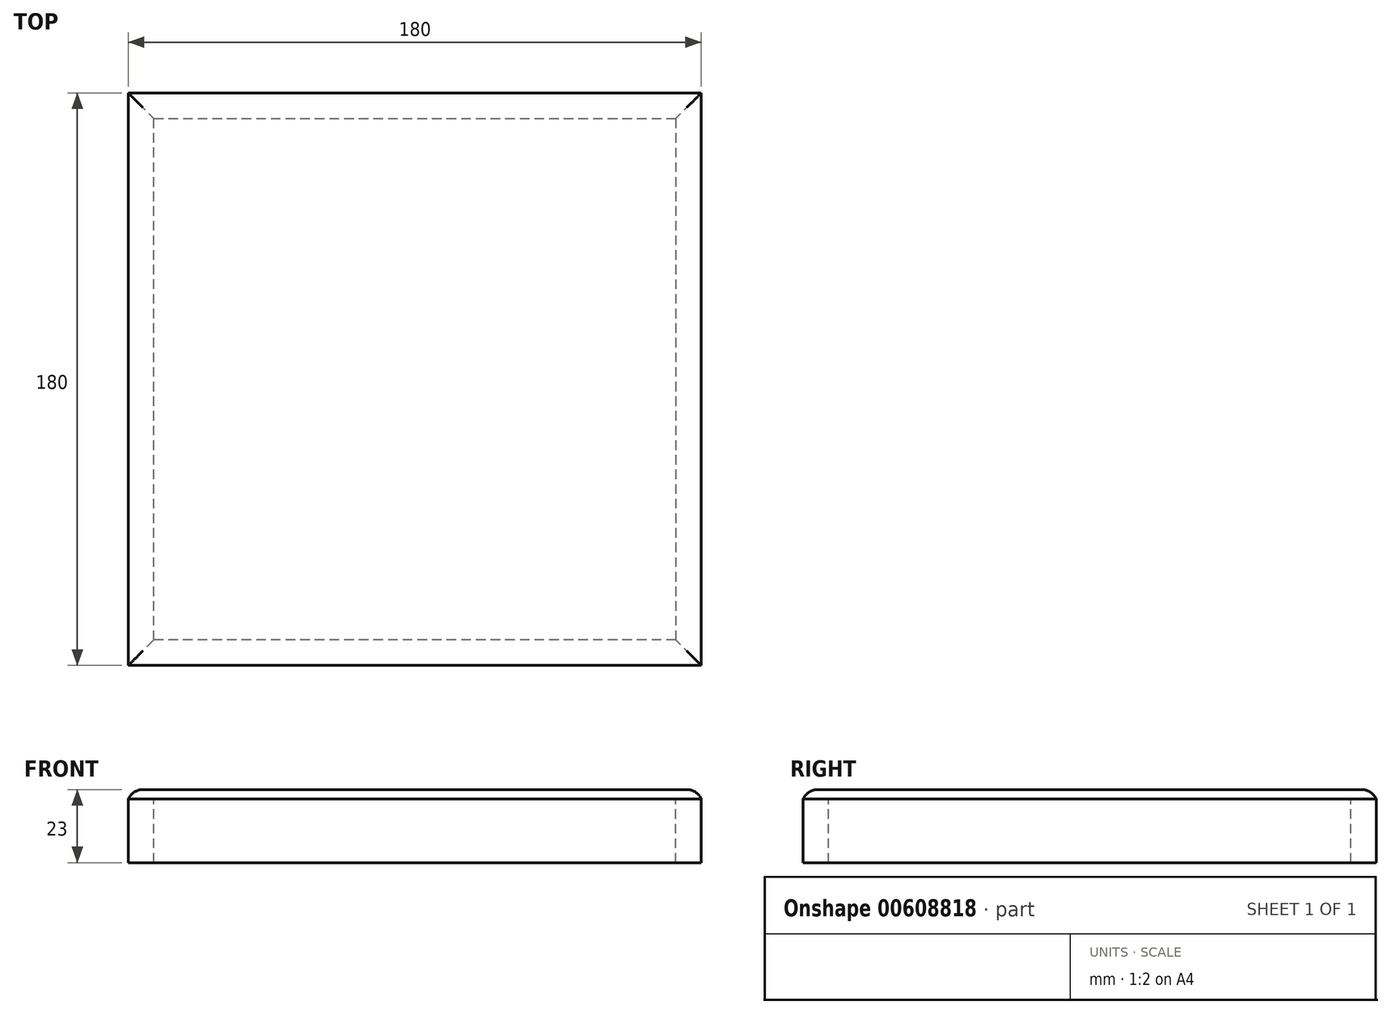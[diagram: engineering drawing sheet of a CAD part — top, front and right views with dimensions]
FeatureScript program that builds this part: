
annotation { "Feature Type Name" : "Feature", "Feature Type Description" : "" }
export const myFeature = defineFeature(function(context is Context, id is Id, definition is map)
    precondition{}
    {
        {
            var Q0;
            Q0=qCreatedBy(makeId("Top.planeOp"),FACE);
            var sketch = newSketch(context, id + "F0", { "sketchPlane" : qUnion([Q0])});
            skLineSegment(sketch, "E0.bottom", {"start": v(0, 0) * mm, "end": v(180, 0) * mm});
            skLineSegment(sketch, "E0.top", {"start": v(0, -180) * mm, "end": v(180, -180) * mm});
            skLineSegment(sketch, "E0.left", {"start": v(0, 0) * mm, "end": v(0, -180) * mm});
            skLineSegment(sketch, "E0.right", {"start": v(180, 0) * mm, "end": v(180, -180) * mm});
            skSolve(sketch);
        }
        {
            var Q0;
            Q0=makeQuery(id+"F0.imprint","IMPRINT",FACE,{"disambiguationData":[TD([[makeQuery(id+"F0.imprint","IMPRINT",EDGE,{"derivedFrom":sQuery(id+"F0.wireOp",EDGE,"E0.bottom")}),-1.0]])]});
            extrude(context, id + "F1", {"entities" : qUnion([Q0]), "oppositeDirection" : true, "depth" : 3 * mm, "offsetDistance" : 25 * mm});
        }
        {
            var Q0;
            Q0=makeQuery(id+"F1.opExtrude","CAP_FACE",FACE,{"disambiguationData":[OSD([sQuery(id+"F0.wireOp",EDGE,"E0.bottom"),sQuery(id+"F0.wireOp",EDGE,"E0.top"),sQuery(id+"F0.wireOp",EDGE,"E0.left"),sQuery(id+"F0.wireOp",EDGE,"E0.right")])],"isStart":false});
            var sketch = newSketch(context, id + "F2", { "sketchPlane" : qUnion([Q0])});
            skLineSegment(sketch, "E1.0", {"start": v(8, 172) * mm, "end": v(8, 8) * mm});
            skLineSegment(sketch, "E1.1", {"start": v(172, 172) * mm, "end": v(8, 172) * mm});
            skLineSegment(sketch, "E1.2", {"start": v(172, 8) * mm, "end": v(172, 172) * mm});
            skLineSegment(sketch, "E1.3", {"start": v(8, 8) * mm, "end": v(172, 8) * mm});
            skLineSegment(sketch, "E2", {"start": v(8, 172) * mm, "end": v(0, 180) * mm});
            skLineSegment(sketch, "E3", {"start": v(180, 180) * mm, "end": v(172, 172) * mm});
            skLineSegment(sketch, "E4", {"start": v(180, 0) * mm, "end": v(172, 8) * mm});
            skLineSegment(sketch, "E5", {"start": v(0, 0) * mm, "end": v(8, 8) * mm});
            skSolve(sketch);
        }
        {
            var Q0;
            Q0=makeQuery(id+"F2.imprint","IMPRINT",FACE,{"disambiguationData":[TD([[makeQuery(id+"F2.imprint","IMPRINT",EDGE,{"derivedFrom":sQuery(id+"F2.wireOp",EDGE,"E1.1")}),-1.0]])]});
            extrude(context, id + "F3", {"entities" : qUnion([Q0]), "depth" : 20 * mm, "offsetDistance" : 25 * mm});
        }
        {
            var Q0;
            Q0=makeQuery(id+"F2.imprint","IMPRINT",FACE,{"disambiguationData":[TD([[makeQuery(id+"F2.imprint","IMPRINT",EDGE,{"derivedFrom":sQuery(id+"F2.wireOp",EDGE,"E1.0")}),-1.0]])]});
            var Q1;
            Q1=makeQuery(id+"F3.opExtrude","CAP_VERTEX",VERTEX,{"disambiguationData":[OSD([sQuery(id+"F0.wireOp",EDGE,"E0.top"),sQuery(id+"F0.wireOp",EDGE,"E0.left"),sQuery(id+"F2.wireOp",EDGE,"E2")])],"isStart":false});
            extrude(context, id + "F4", {"entities" : qUnion([Q0]), "endBound" : BoundingType.UP_TO_VERTEX, "depth" : 25 * mm, "endBoundEntityVertex" : qUnion([Q1]), "offsetDistance" : 25 * mm});
        }
        {
            var Q0;
            Q0=makeQuery(id+"F2.imprint","IMPRINT",FACE,{"disambiguationData":[TD([[makeQuery(id+"F2.imprint","IMPRINT",EDGE,{"derivedFrom":sQuery(id+"F2.wireOp",EDGE,"E1.2")}),-1.0]])]});
            var Q1;
            Q1=makeQuery(id+"F3.opExtrude","CAP_VERTEX",VERTEX,{"disambiguationData":[OSD([sQuery(id+"F2.wireOp",EDGE,"E1.1"),sQuery(id+"F2.wireOp",EDGE,"E1.2"),sQuery(id+"F2.wireOp",EDGE,"E3")])],"isStart":false});
            extrude(context, id + "F5", {"entities" : qUnion([Q0]), "endBound" : BoundingType.UP_TO_VERTEX, "depth" : 25 * mm, "endBoundEntityVertex" : qUnion([Q1]), "offsetDistance" : 25 * mm});
        }
        {
            var Q0;
            Q0=makeQuery(id+"F2.imprint","IMPRINT",FACE,{"disambiguationData":[TD([[makeQuery(id+"F2.imprint","IMPRINT",EDGE,{"derivedFrom":sQuery(id+"F2.wireOp",EDGE,"E1.3")}),-1.0]])]});
            var Q1;
            Q1=makeQuery(id+"F5.opExtrude","CAP_VERTEX",VERTEX,{"disambiguationData":[OSD([sQuery(id+"F2.wireOp",EDGE,"E1.2"),sQuery(id+"F2.wireOp",EDGE,"E1.3"),sQuery(id+"F2.wireOp",EDGE,"E4"),dummyQuery(id+"F5.vertexPlane.planeOp",FACE)])],"isStart":false});
            extrude(context, id + "F6", {"entities" : qUnion([Q0]), "endBound" : BoundingType.UP_TO_VERTEX, "depth" : 25 * mm, "endBoundEntityVertex" : qUnion([Q1]), "offsetDistance" : 25 * mm});
        }
        {
            var Q0;
            Q0=makeQuery(id+"F1.opExtrude","CAP_EDGE",EDGE,{"disambiguationData":[OSD([sQuery(id+"F0.wireOp",EDGE,"E0.top")])],"isStart":true});
            var Q1;
            Q1=makeQuery(id+"F1.opExtrude","CAP_EDGE",EDGE,{"disambiguationData":[OSD([sQuery(id+"F0.wireOp",EDGE,"E0.right")])],"isStart":true});
            var Q2;
            Q2=makeQuery(id+"F1.opExtrude","CAP_EDGE",EDGE,{"disambiguationData":[OSD([sQuery(id+"F0.wireOp",EDGE,"E0.bottom")])],"isStart":true});
            var Q3;
            Q3=makeQuery(id+"F1.opExtrude","CAP_EDGE",EDGE,{"disambiguationData":[OSD([sQuery(id+"F0.wireOp",EDGE,"E0.left")])],"isStart":true});
            fillet(context, id + "F7", {"entities" : qUnion([Q0, Q1, Q2, Q3]), "radius" : 5 * mm, "tangentPropagation" : true, "allowEdgeOverflow" : false});
        }
    });
